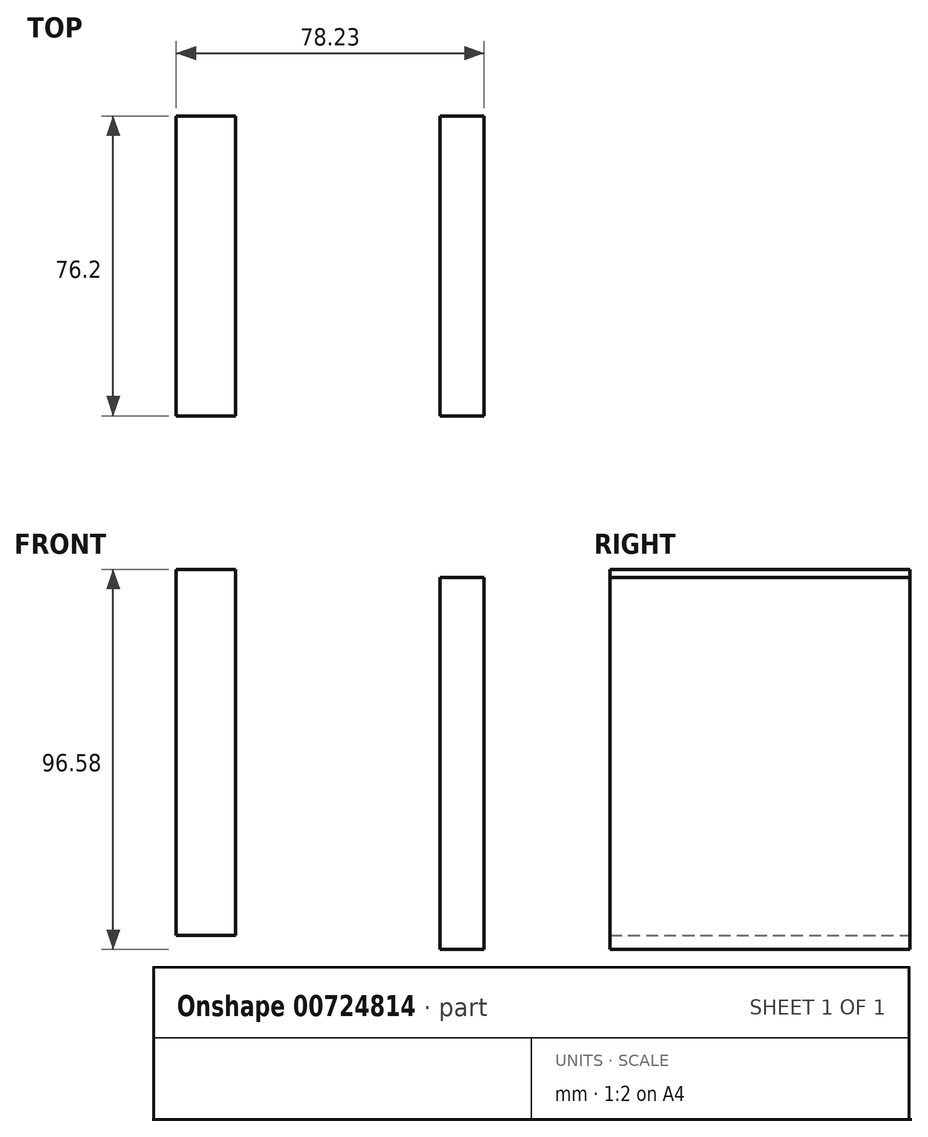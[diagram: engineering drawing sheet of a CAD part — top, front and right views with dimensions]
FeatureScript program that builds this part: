
annotation { "Feature Type Name" : "Feature", "Feature Type Description" : "" }
export const myFeature = defineFeature(function(context is Context, id is Id, definition is map)
    precondition{}
    {
        {
            var Q0;
            Q0=qCreatedBy(makeId("Front.planeOp"),FACE);
            var sketch = newSketch(context, id + "F0", { "sketchPlane" : qUnion([Q0])});
            skLineSegment(sketch, "E0.bottom", {"start": v(-58.48, 49.82) * mm, "end": v(-43.44, 49.82) * mm});
            skLineSegment(sketch, "E0.top", {"start": v(-58.48, -43.2) * mm, "end": v(-43.44, -43.2) * mm});
            skLineSegment(sketch, "E0.left", {"start": v(-58.48, 49.82) * mm, "end": v(-58.48, -43.2) * mm});
            skLineSegment(sketch, "E0.right", {"start": v(-43.44, 49.82) * mm, "end": v(-43.44, -43.2) * mm});
            skLineSegment(sketch, "E1.bottom", {"start": v(8.54, 47.78) * mm, "end": v(19.75, 47.78) * mm});
            skLineSegment(sketch, "E1.top", {"start": v(8.54, -46.76) * mm, "end": v(19.75, -46.76) * mm});
            skLineSegment(sketch, "E1.left", {"start": v(8.54, 47.78) * mm, "end": v(8.54, -46.76) * mm});
            skLineSegment(sketch, "E1.right", {"start": v(19.75, 47.78) * mm, "end": v(19.75, -46.76) * mm});
            skSolve(sketch);
        }
        {
            var Q0;
            Q0=makeQuery(id+"F0.imprint","IMPRINT",FACE,{"disambiguationData":[TD([[makeQuery(id+"F0.imprint","IMPRINT",EDGE,{"derivedFrom":sQuery(id+"F0.wireOp",EDGE,"E0.bottom")}),-1.0]])]});
            var Q1;
            Q1=makeQuery(id+"F0.imprint","IMPRINT",FACE,{"disambiguationData":[TD([[makeQuery(id+"F0.imprint","IMPRINT",EDGE,{"derivedFrom":sQuery(id+"F0.wireOp",EDGE,"E1.bottom")}),-1.0]])]});
            extrude(context, id + "F1", {"entities" : qUnion([Q0, Q1]), "depth" : 76.2 * mm, "offsetDistance" : 25.4 * mm});
        }
    });
